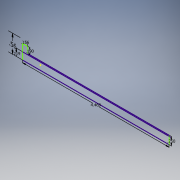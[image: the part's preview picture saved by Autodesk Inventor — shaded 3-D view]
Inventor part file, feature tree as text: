
AUTODESK INVENTOR PART (.ipt)
format: ipt  version: 2018 (Build 220112000, 112)  size: 97,280 bytes
history: native  units: in
note: dims shown in document units (in); Inventor stores cm internally (conversion verified against a paired STEP export)
features: other x2, sketch x1
ambient origin geometry x8: Origin, YZ Plane, XZ Plane, XY Plane, X Axis, Y Axis, Z Axis, Center Point
feature tree (3):
  other  "Annotations"
  sketch  "Sketch2"  dims[d17=4.469in d18=0.25in d19=0.156in d20=0.19in d22=0.2188in d21=0.5567in]
  other  "Linear Dimension 1"
